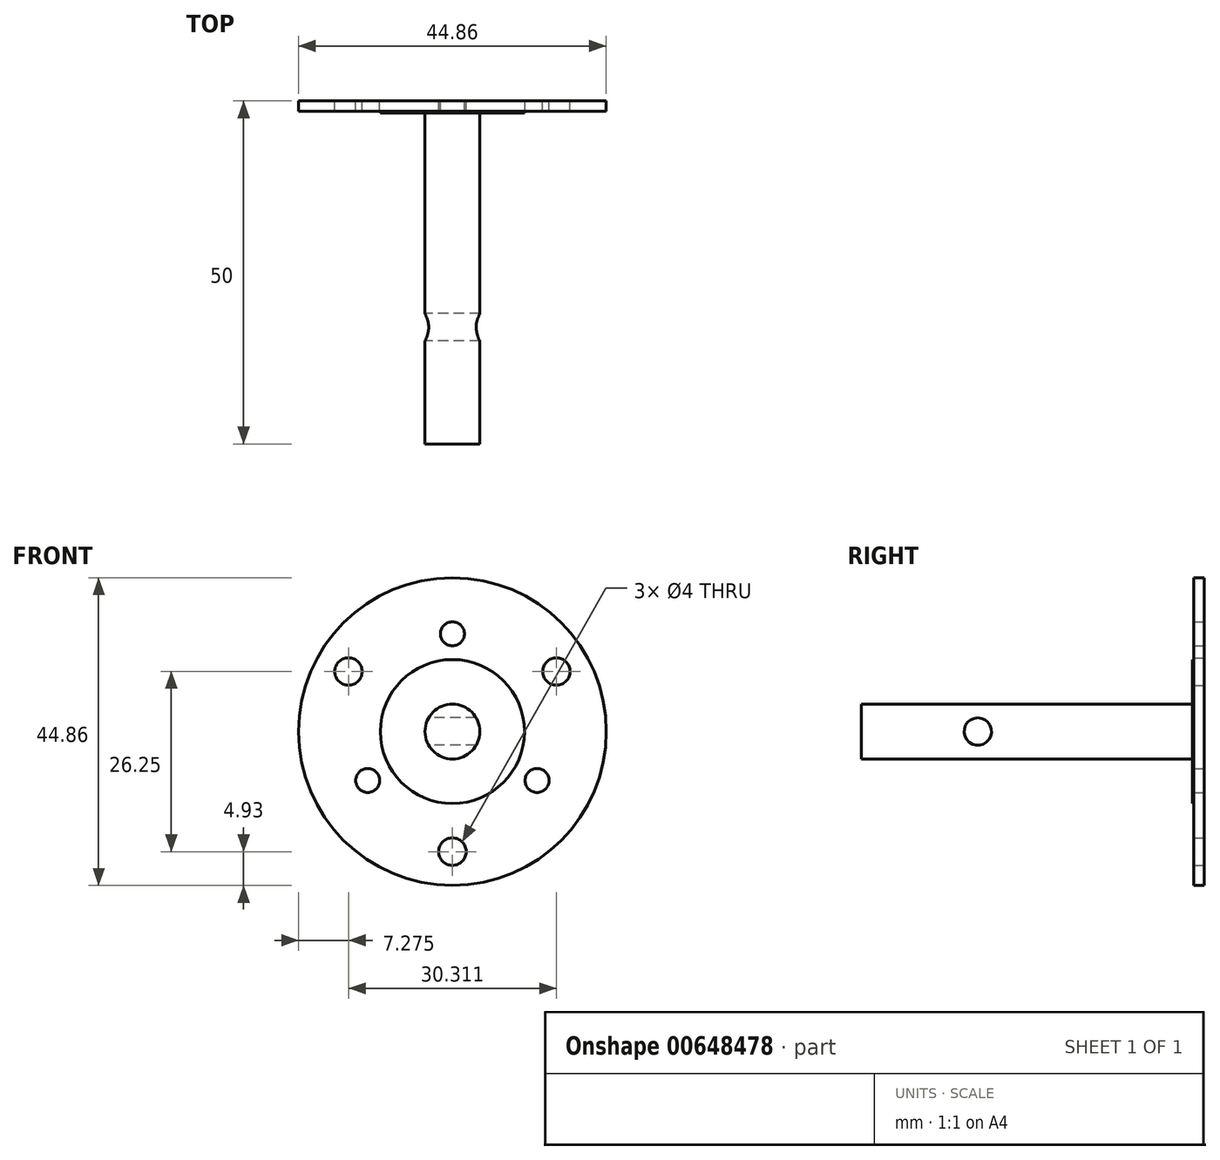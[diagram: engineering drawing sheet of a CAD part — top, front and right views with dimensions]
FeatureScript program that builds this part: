
annotation { "Feature Type Name" : "Feature", "Feature Type Description" : "" }
export const myFeature = defineFeature(function(context is Context, id is Id, definition is map)
    precondition{}
    {
        {
            var Q0;
            Q0=qCreatedBy(makeId("Front.planeOp"),FACE);
            var sketch = newSketch(context, id + "F0", { "sketchPlane" : qUnion([Q0])});
            skCircle(sketch, "E0", {"center": v(0, 0) * mm, "radius": 22.43 * mm});
            skSolve(sketch);
        }
        {
            var Q0;
            Q0=makeQuery(id+"F0.imprint","IMPRINT",FACE,{"disambiguationData":[TD([[makeQuery(id+"F0.imprint","IMPRINT",EDGE,{"derivedFrom":sQuery(id+"F0.wireOp",EDGE,"E0")}),1.0]])]});
            var Q1;
            Q1=sQuery(id+"F0.wireOp",EDGE,"E0");
            extrude(context, id + "F1", {"entities" : qUnion([Q0]), "surfaceEntities" : qUnion([Q1]), "depth" : 1.5 * mm, "offsetDistance" : 25 * mm});
        }
        {
            var Q0;
            Q0=makeQuery(id+"F1.opExtrude","CAP_FACE",FACE,{"disambiguationData":[OSD([sQuery(id+"F0.wireOp",EDGE,"E0")])],"isStart":false});
            var sketch = newSketch(context, id + "F2", { "sketchPlane" : qUnion([Q0])});
            skCircle(sketch, "E1", {"center": v(0, 0) * mm, "radius": 10.5 * mm});
            skSolve(sketch);
        }
        {
            var Q0;
            Q0 = qSketchRegion(id + "F2", true);
            extrude(context, id + "F3", {"entities" : qUnion([Q0]), "operationType" : NewBodyOperationType.ADD, "depth" : 0.25 * mm, "offsetDistance" : 25 * mm});
        }
        {
            var Q0;
            Q0=makeQuery(id+"F3.opExtrude","CAP_FACE",FACE,{"disambiguationData":[OSD([sQuery(id+"F2.wireOp",EDGE,"E1")])],"isStart":false});
            var sketch = newSketch(context, id + "F4", { "sketchPlane" : qUnion([Q0])});
            skCircle(sketch, "E2", {"center": v(0, 0) * mm, "radius": 4 * mm});
            skSolve(sketch);
        }
        {
            var Q0;
            Q0 = qSketchRegion(id + "F4", true);
            extrude(context, id + "F5", {"entities" : qUnion([Q0]), "operationType" : NewBodyOperationType.ADD, "depth" : 48.25 * mm, "offsetDistance" : 25 * mm});
        }
        {
            var Q0;
            Q0=qCreatedBy(makeId("Right.planeOp"),FACE);
            var sketch = newSketch(context, id + "F6", { "sketchPlane" : qUnion([Q0])});
            skPoint(sketch, "E3", {"position": v(-33, 0) * mm});
            skSolve(sketch);
        }
        {
            var Q0;
            Q0=sQuery(id+"F6.wireOp",VERTEX,"E3");
            var Q1;
            Q1=makeQuery(id+"F1.opExtrude","SWEPT_BODY",BODY,{"disambiguationData":[OSD([sQuery(id+"F0.wireOp",EDGE,"E0")])]});
            hole(context, id + "F7", {"style" : HoleStyle.SIMPLE, "endStyle" : HoleEndStyle.THROUGH, "oppositeDirection" : true, "holeDiameter" : 4 * mm, "majorDiameter" : 5 * mm, "isTappedThrough" : true, "tappedDepth" : 12 * mm, "tapClearance" : 3, "locations" : qUnion([Q0]), "scope" : qUnion([Q1])});
        }
        {
            var Q0;
            Q0=qCreatedBy(makeId("Right.planeOp"),FACE);
            var sketch = newSketch(context, id + "F8", { "sketchPlane" : qUnion([Q0])});
            skPoint(sketch, "E4", {"position": v(-33, 0) * mm});
            skSolve(sketch);
        }
        {
            var Q0;
            Q0=sQuery(id+"F8.wireOp",VERTEX,"E4");
            var Q1;
            Q1=makeQuery(id+"F1.opExtrude","SWEPT_BODY",BODY,{"disambiguationData":[OSD([sQuery(id+"F0.wireOp",EDGE,"E0")])]});
            hole(context, id + "F9", {"style" : HoleStyle.SIMPLE, "endStyle" : HoleEndStyle.THROUGH, "holeDiameter" : 4 * mm, "majorDiameter" : 5 * mm, "isTappedThrough" : true, "tappedDepth" : 12 * mm, "tapClearance" : 3, "locations" : qUnion([Q0]), "scope" : qUnion([Q1])});
        }
        {
            var Q0;
            Q0=makeQuery(id+"F1.opExtrude","CAP_FACE",FACE,{"disambiguationData":[OSD([sQuery(id+"F0.wireOp",EDGE,"E0")])],"isStart":true});
            var sketch = newSketch(context, id + "F10", { "sketchPlane" : qUnion([Q0])});
            skPoint(sketch, "E5", {"position": v(0, 14.25) * mm});
            skPoint(sketch, "E6.1.0", {"position": v(-12.34, -7.12) * mm});
            skPoint(sketch, "E6.2.0", {"position": v(12.34, -7.13) * mm});
            skPoint(sketch, "E6.center", {"position": v(0, 0) * mm});
            skSolve(sketch);
        }
        {
            var Q0;
            Q0=sQuery(id+"F10.wireOp",VERTEX,"E5");
            var Q1;
            Q1=sQuery(id+"F10.wireOp",VERTEX,"E6.1.0");
            var Q2;
            Q2=sQuery(id+"F10.wireOp",VERTEX,"E6.2.0");
            var Q3;
            Q3=makeQuery(id+"F1.opExtrude","SWEPT_BODY",BODY,{"disambiguationData":[OSD([sQuery(id+"F0.wireOp",EDGE,"E0")])]});
            hole(context, id + "F11", {"style" : HoleStyle.SIMPLE, "endStyle" : HoleEndStyle.THROUGH, "holeDiameter" : 3.5 * mm, "majorDiameter" : 5 * mm, "isTappedThrough" : true, "tappedDepth" : 12 * mm, "tapClearance" : 3, "locations" : qUnion([Q0, Q1, Q2]), "scope" : qUnion([Q3])});
        }
        {
            var Q0;
            Q0=makeQuery(id+"F1.opExtrude","CAP_FACE",FACE,{"disambiguationData":[OSD([sQuery(id+"F0.wireOp",EDGE,"E0")])],"isStart":true});
            var sketch = newSketch(context, id + "F12", { "sketchPlane" : qUnion([Q0])});
            skPoint(sketch, "E7", {"position": v(0, -17.5) * mm});
            skPoint(sketch, "E8.1.0", {"position": v(15.16, 8.75) * mm});
            skPoint(sketch, "E8.2.0", {"position": v(-15.16, 8.75) * mm});
            skPoint(sketch, "E8.center", {"position": v(0, 0) * mm});
            skSolve(sketch);
        }
        {
            var Q0;
            Q0=sQuery(id+"F12.wireOp",VERTEX,"E8.2.0");
            var Q1;
            Q1=sQuery(id+"F12.wireOp",VERTEX,"E7");
            var Q2;
            Q2=sQuery(id+"F12.wireOp",VERTEX,"E8.1.0");
            var Q3;
            Q3=makeQuery(id+"F1.opExtrude","SWEPT_BODY",BODY,{"disambiguationData":[OSD([sQuery(id+"F0.wireOp",EDGE,"E0")])]});
            hole(context, id + "F13", {"style" : HoleStyle.SIMPLE, "endStyle" : HoleEndStyle.THROUGH, "holeDiameter" : 4 * mm, "majorDiameter" : 5 * mm, "isTappedThrough" : true, "tappedDepth" : 12 * mm, "tapClearance" : 3, "locations" : qUnion([Q0, Q1, Q2]), "scope" : qUnion([Q3])});
        }
    });
